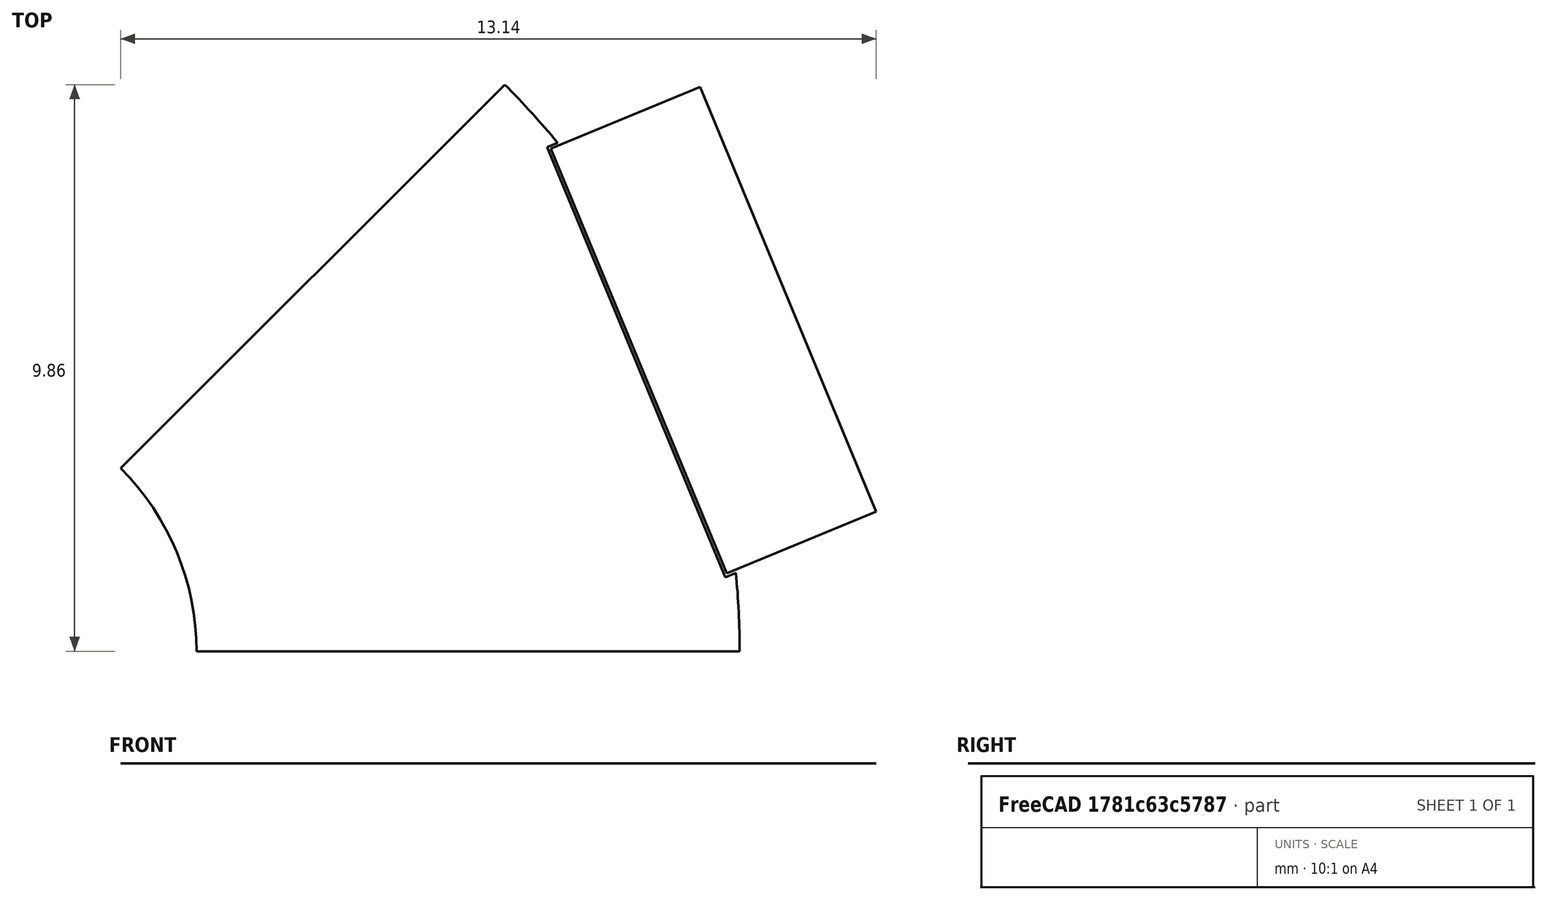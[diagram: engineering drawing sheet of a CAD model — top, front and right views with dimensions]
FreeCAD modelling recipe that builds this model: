
FCSTD DOCUMENT  (FreeCAD 0.18R4 (GitTag))
Label: rotor5
License: All rights reserved
LicenseURL: http://en.wikipedia.org/wiki/All_rights_reserved
objects: Sketcher::SketchObject×5, PartDesign::Body×2, Surface::Filling×2, Spreadsheet::Sheet×1
note: 9 computed .brp shape members not serialized (recipe doc carries the construction recipe); baked Part::Feature solids carry a one-line shape summary decoded from their .brp

FEATURE [Spreadsheet::Sheet] Spreadsheet  label="Variables"
  cells = A2=poleNumber; B2(poleNumber)=8; A3=outerDiameter; B3(outerDiameter)=33; D3=Calc Value; A4=innerDiameter; B4(innerDiameter)=9; D4=Input Value; A5=stackLength; B5(stackLength)=20; A6=stackingFactor; B6(stackingFactor)=0.95; A7=embrace; B7(embrace)=70; A8=contourRatio; B8(contourRatio)=80; A9=magnetAirgap; B9(magnetAirgap)=0.05; A10=poleSeparation; B10(poleSeparation)=2; A11=magnetWidth; B11(magnetWidth)=8; A12=magnetHeight; B12(magnetHeight)=2.8; A13=rib; B13(rib)=0.5; A14=bridgeCurved; B14(bridgeCurved)=0.5; A15=cutTop; B15(cutTop)=0.2; A16=cutBottom; B16(cutBottom)=0.25; A17=segmentAngle; B17(segmentAngle)==360 / poleNumber; A18=movePocketInwards; B18(movePocketInwards)=0.5; A19=cuttingThickness; B19(cuttingThickness)=0.1; A20=magnetLength; B20(magnetLength)==stackLength; A21=cut; B21(cut)=0.2; A22=ribShaft; B22(ribShaft)=0.5; A23=magnetEmbrace; B23(magnetEmbrace)=70; A24=magnetContourRatio; B24(magnetContourRatio)=95; A25=axialMisalignment; B25(axialMisalignment)=0.5
FEATURE [Sketcher::SketchObject] Sketch003  label="RotorSketch"
  MapMode = 5
  Support = -> [XY_Plane]
  expr: Constraints[33] = Variables.magnetWidth + 2 * Variables.magnetAirgap
  expr: Constraints[15] = Variables.outerDiameter / 2
  expr: Constraints[32] = Spreadsheet.cut
  expr: Constraints[50] = Variables.magnetHeight + Variables.magnetAirgap
  expr: Constraints[18] = Variables.segmentAngle / 2
  expr: Constraints[0] = Variables.segmentAngle
  expr: Constraints[14] = Variables.innerDiameter / 2
  sketch-geometry (19):
    g0: LineSegment [constr] StartX=4.5 StartY=0 StartZ=0 EndX=16.5 EndY=0 EndZ=0
    g1: LineSegment [constr] StartX=3.18198 StartY=3.18198 StartZ=0 EndX=11.6673 EndY=11.6673 EndZ=0
    g2: LineSegment [constr] StartX=0 StartY=0 StartZ=0 EndX=4.5 EndY=0 EndZ=0
    g3: LineSegment [constr] StartX=0 StartY=0 StartZ=0 EndX=3.18198 EndY=3.18198 EndZ=0
    g4: ArcOfCircle [constr] CenterX=0 CenterY=0 CenterZ=0 NormalX=0 NormalY=0 NormalZ=1 AngleXU=0 Radius=16.5 StartAngle=0 EndAngle=0.785398
    g5: ArcOfCircle CenterX=0 CenterY=0 CenterZ=0 NormalX=0 NormalY=0 NormalZ=1 AngleXU=0 Radius=4.5 StartAngle=0 EndAngle=0.785398
    g6: LineSegment [constr] StartX=0 StartY=0 StartZ=0 EndX=15.244 EndY=6.31428 EndZ=0
    g7: LineSegment [constr] StartX=0 StartY=0 StartZ=0 EndX=12.7091 EndY=10.5228 EndZ=0
    g8: LineSegment [constr] StartX=0 StartY=0 StartZ=0 EndX=16.4274 EndY=1.54594 EndZ=0
    g9: LineSegment [constr] StartX=0 StartY=0 StartZ=0 EndX=10.5947 EndY=8.77218 EndZ=0
    g10: LineSegment [constr] StartX=0 StartY=0 StartZ=0 EndX=13.6945 EndY=1.28875 EndZ=0
    g11: LineSegment StartX=10.5947 StartY=8.77218 StartZ=0 EndX=13.6945 EndY=1.28875 EndZ=0
    g12: LineSegment StartX=10.5947 StartY=8.77218 StartZ=0 EndX=10.7795 EndY=8.84871 EndZ=0
    g13: ArcOfCircle CenterX=0 CenterY=0 CenterZ=0 NormalX=0 NormalY=0 NormalZ=1 AngleXU=0 Radius=13.9462 StartAngle=0.687345 EndAngle=0.785398
    g14: LineSegment StartX=3.18198 StartY=3.18198 StartZ=0 EndX=9.86148 EndY=9.86148 EndZ=0
    g15: LineSegment StartX=4.5 StartY=0 StartZ=0 EndX=13.9462 EndY=0 EndZ=0
    g16: LineSegment StartX=13.6945 StartY=1.28875 StartZ=0 EndX=13.8793 EndY=1.36529 EndZ=0
    g17: ArcOfCircle CenterX=0 CenterY=0 CenterZ=0 NormalX=0 NormalY=0 NormalZ=1 AngleXU=0 Radius=13.9462 StartAngle=0 EndAngle=0.0980535
    g18: LineSegment [constr] StartX=10.5947 StartY=8.77218 StartZ=0 EndX=13.2278 EndY=9.86282 EndZ=0
  constraints (51):
    c: Angle(g0,g1) = 0.785398
    c: Coincident(g2,g-1)
    c: Coincident(g2,g0)
    c: Coincident(g3,g2)
    c: Coincident(g3,g1)
    c: Parallel(g2,g0)
    c: Parallel(g3,g1)
    c: Coincident(g4,g-1)
    c: Coincident(g4,g0)
    c: Coincident(g4,g1)
    c: Coincident(g5,g4)
    c: Coincident(g5,g1)
    c: Coincident(g5,g0)
    c: Angle(g-1,g2) = 0
    c: Radius(g5) = 4.5
    c: Radius(g4) = 16.5
    c: Coincident(g6,g5)
    c: PointOnObject(g6,g4)
    c: Angle(g-1,g6) = 0.392699
    c: Coincident(g7,g5)
    c: PointOnObject(g7,g4)
    c: Coincident(g8,g5)
    c: Symmetric(g7,g8,g6)
    c: Coincident(g9,g5)
    c: PointOnObject(g9,g7)
    c: Coincident(g10,g5)
    c: PointOnObject(g10,g8)
    c: Equal(g9,g10)
    c: Coincident(g11,g9)
    c: Coincident(g11,g10)
    c: Coincident(g12,g11)
    c: Angle(g11,g12) = 1.5708
    c: Distance(g12) = 0.2
    c: Distance(g11) = 8.1
    c: Coincident(g13,g5)
    c: Coincident(g13,g12)
    c: PointOnObject(g13,g1)
    c: PointOnObject(g15,g0)
    c: Coincident(g14,g5)
    c: Coincident(g14,g13)
    c: Coincident(g15,g5)
    c: Coincident(g16,g11)
    c: Angle(g16,g11) = 1.5708
    c: Equal(g16,g12)
    c: Coincident(g17,g5)
    c: Coincident(g17,g15)
    c: Coincident(g17,g16)
    c: Coincident(g18,g11)
    c: PointOnObject(g18,g4)
    c: Angle(g11,g18) = 1.5708
    c: Distance(g18) = 2.85
FEATURE [Sketcher::SketchObject] Sketch004  label="BoundingBox"
  MapMode = 5
  Support = -> [XY_Plane]
  expr: Constraints[8] = Variables.outerDiameter
  sketch-geometry (6):
    g0: LineSegment StartX=-16.5 StartY=-16.5 StartZ=0 EndX=16.5 EndY=-16.5 EndZ=0
    g1: LineSegment StartX=16.5 StartY=-16.5 StartZ=0 EndX=16.5 EndY=16.5 EndZ=0
    g2: LineSegment StartX=16.5 StartY=16.5 StartZ=0 EndX=-16.5 EndY=16.5 EndZ=0
    g3: LineSegment StartX=-16.5 StartY=16.5 StartZ=0 EndX=-16.5 EndY=-16.5 EndZ=0
    g4: LineSegment [constr] StartX=-16.5 StartY=-16.5 StartZ=0 EndX=16.5 EndY=16.5 EndZ=0
    g5: GeomPoint X=0 Y=0 Z=0
  constraints (14):
    c: Coincident(g0,g1)
    c: Coincident(g1,g2)
    c: Coincident(g2,g3)
    c: Coincident(g3,g0)
    c: Horizontal(g0)
    c: Horizontal(g2)
    c: Vertical(g1)
    c: Vertical(g3)
    c: DistanceY(g1,g1) = 33
    c: Equal(g2,g1)
    c: Coincident(g4,g0)
    c: Coincident(g4,g1)
    c: Symmetric(g0,g1,g5)
    c: Coincident(g-1,g5)
FEATURE [Sketcher::SketchObject] Sketch005  label="RotorSideSketch"
  MapMode = 5
  Support = -> [XY_Plane001]
  expr: Constraints[21] = Variables.stackLength / 2 - Variables.axialMisalignment
  expr: Constraints[9] = Variables.outerDiameter / 2
  expr: Constraints[8] = Variables.innerDiameter / 2
  expr: Constraints[7] = Variables.stackLength
  sketch-geometry (8):
    g0: LineSegment StartX=-9.5 StartY=4.5 StartZ=0 EndX=10.5 EndY=4.5 EndZ=0
    g1: LineSegment StartX=10.5 StartY=4.5 StartZ=0 EndX=10.5 EndY=16.5 EndZ=0
    g2: LineSegment StartX=10.5 StartY=16.5 StartZ=0 EndX=-9.5 EndY=16.5 EndZ=0
    g3: LineSegment StartX=-9.5 StartY=16.5 StartZ=0 EndX=-9.5 EndY=4.5 EndZ=0
    g4: LineSegment StartX=-9.5 StartY=-4.5 StartZ=0 EndX=10.5 EndY=-4.5 EndZ=0
    g5: LineSegment StartX=10.5 StartY=-4.5 StartZ=0 EndX=10.5 EndY=-16.5 EndZ=0
    g6: LineSegment StartX=10.5 StartY=-16.5 StartZ=0 EndX=-9.5 EndY=-16.5 EndZ=0
    g7: LineSegment StartX=-9.5 StartY=-16.5 StartZ=0 EndX=-9.5 EndY=-4.5 EndZ=0
  constraints (23):
    c: Coincident(g0,g1)
    c: Coincident(g1,g2)
    c: Coincident(g2,g3)
    c: Coincident(g3,g0)
    c: Horizontal(g0)
    c: Vertical(g1)
    c: Vertical(g3)
    c: DistanceX(g2,g2) = 20
    c: DistanceY(g-1,g0) = 4.5
    c: DistanceY(g-1,g1) = 16.5
    c: Coincident(g4,g5)
    c: Coincident(g5,g6)
    c: Coincident(g6,g7)
    c: Coincident(g7,g4)
    c: Horizontal(g4)
    c: Vertical(g5)
    c: Vertical(g7)
    c: Equal(g4,g0)
    c: Equal(g7,g3)
    c: Horizontal(g6)
    c: Horizontal(g2)
    c: DistanceX(g0,g-1) = 9.5
    c: Symmetric(g4,g0,g-1)
FEATURE [Sketcher::SketchObject] Sketch006  label="MagnetSideSketch"
  ExternalGeometry = -> [Sketch005]
  MapMode = 5
  Support = -> [XY_Plane001]
  expr: Constraints[20] = Variables.stackLength / 2 - Variables.axialMisalignment
  expr: Constraints[7] = Variables.magnetHeight
  sketch-geometry (8):
    g0: LineSegment StartX=-9.5 StartY=13.7 StartZ=0 EndX=10.5 EndY=13.7 EndZ=0
    g1: LineSegment StartX=10.5 StartY=13.7 StartZ=0 EndX=10.5 EndY=16.5 EndZ=0
    g2: LineSegment StartX=10.5 StartY=16.5 StartZ=0 EndX=-9.5 EndY=16.5 EndZ=0
    g3: LineSegment StartX=-9.5 StartY=16.5 StartZ=0 EndX=-9.5 EndY=13.7 EndZ=0
    g4: LineSegment StartX=-9.5 StartY=-16.5 StartZ=0 EndX=10.5 EndY=-16.5 EndZ=0
    g5: LineSegment StartX=10.5 StartY=-16.5 StartZ=0 EndX=10.5 EndY=-13.7 EndZ=0
    g6: LineSegment StartX=10.5 StartY=-13.7 StartZ=0 EndX=-9.5 EndY=-13.7 EndZ=0
    g7: LineSegment StartX=-9.5 StartY=-13.7 StartZ=0 EndX=-9.5 EndY=-16.5 EndZ=0
  constraints (21):
    c: Coincident(g0,g1)
    c: Coincident(g1,g2)
    c: Coincident(g2,g3)
    c: Coincident(g3,g0)
    c: Horizontal(g0)
    c: Vertical(g1)
    c: Vertical(g3)
    c: DistanceY(g1,g1) = 2.8
    c: Coincident(g4,g5)
    c: Coincident(g5,g6)
    c: Coincident(g6,g7)
    c: Coincident(g7,g4)
    c: Horizontal(g4)
    c: Vertical(g5)
    c: Vertical(g7)
    c: Symmetric(g6,g0,g-1)
    c: Symmetric(g5,g0,g-1)
    c: Equal(g7,g3)
    c: Coincident(g1,g-3)
    c: Horizontal(g2)
    c: DistanceX(g0,g-1) = 9.5
FEATURE [PartDesign::Body] Body001  label="SideView"
  Group = -> [Sketch005,Sketch006]
  Origin = -> Origin001
FEATURE [Surface::Filling] Surface  label="Rotor_Surface"
  Anisotropy = false
  BoundaryEdges = -> [Sketch003]
  BoundaryOrder = [0,0,0,0,0,0,0,0]
  Degree = 3
  Iterations = 2
  MaximumDegree = 8
  MaximumSegments = 9
  PointsOnCurve = 15
  TolAngular = 0.01
  TolCurvature = 0.1
  Tolerance2d = 1e-05
  Tolerance3d = 0.0001
FEATURE [Sketcher::SketchObject] Sketch007  label="MagnetSketch"
  MapMode = 5
  Support = -> [XY_Plane]
  expr: Constraints[55] = Variables.magnetAirgap
  expr: Constraints[14] = Variables.innerDiameter / 2
  expr: Constraints[33] = Variables.magnetWidth + 2 * Variables.magnetAirgap
  expr: Constraints[15] = Variables.outerDiameter / 2
  expr: Constraints[32] = Spreadsheet.cut
  expr: Constraints[50] = Variables.magnetHeight + Variables.magnetAirgap
  expr: Constraints[18] = Variables.segmentAngle / 2
  expr: Constraints[0] = Variables.segmentAngle
  sketch-geometry (25):
    g0: LineSegment [constr] StartX=4.5 StartY=0 StartZ=0 EndX=16.5 EndY=0 EndZ=0
    g1: LineSegment [constr] StartX=3.18198 StartY=3.18198 StartZ=0 EndX=11.6673 EndY=11.6673 EndZ=0
    g2: LineSegment [constr] StartX=0 StartY=0 StartZ=0 EndX=4.5 EndY=0 EndZ=0
    g3: LineSegment [constr] StartX=0 StartY=0 StartZ=0 EndX=3.18198 EndY=3.18198 EndZ=0
    g4: ArcOfCircle [constr] CenterX=0 CenterY=0 CenterZ=0 NormalX=0 NormalY=0 NormalZ=1 AngleXU=0 Radius=16.5 StartAngle=0 EndAngle=0.785398
    g5: ArcOfCircle [constr] CenterX=0 CenterY=0 CenterZ=0 NormalX=0 NormalY=0 NormalZ=1 AngleXU=0 Radius=4.5 StartAngle=0 EndAngle=0.785398
    g6: LineSegment [constr] StartX=0 StartY=0 StartZ=0 EndX=15.244 EndY=6.31428 EndZ=0
    g7: LineSegment [constr] StartX=0 StartY=0 StartZ=0 EndX=12.7091 EndY=10.5228 EndZ=0
    g8: LineSegment [constr] StartX=0 StartY=0 StartZ=0 EndX=16.4274 EndY=1.54594 EndZ=0
    g9: LineSegment [constr] StartX=0 StartY=0 StartZ=0 EndX=10.5947 EndY=8.77218 EndZ=0
    g10: LineSegment [constr] StartX=0 StartY=0 StartZ=0 EndX=13.6945 EndY=1.28875 EndZ=0
    g11: LineSegment [constr] StartX=10.5947 StartY=8.77218 StartZ=0 EndX=13.6945 EndY=1.28875 EndZ=0
    g12: LineSegment [constr] StartX=10.5947 StartY=8.77218 StartZ=0 EndX=10.7795 EndY=8.84871 EndZ=0
    g13: ArcOfCircle [constr] CenterX=0 CenterY=0 CenterZ=0 NormalX=0 NormalY=0 NormalZ=1 AngleXU=0 Radius=13.9462 StartAngle=0.687345 EndAngle=0.785398
    g14: LineSegment [constr] StartX=3.18198 StartY=3.18198 StartZ=0 EndX=9.86148 EndY=9.86148 EndZ=0
    g15: LineSegment [constr] StartX=4.5 StartY=0 StartZ=0 EndX=13.9462 EndY=0 EndZ=0
    g16: LineSegment StartX=13.6945 StartY=1.28875 StartZ=0 EndX=13.8793 EndY=1.36529 EndZ=0
    g17: ArcOfCircle [constr] CenterX=0 CenterY=0 CenterZ=0 NormalX=0 NormalY=0 NormalZ=1 AngleXU=0 Radius=13.9462 StartAngle=0 EndAngle=0.0980535
    g18: LineSegment [constr] StartX=10.5947 StartY=8.77218 StartZ=0 EndX=13.2278 EndY=9.86282 EndZ=0
    g19: LineSegment StartX=10.6601 StartY=8.74512 StartZ=0 EndX=13.7215 EndY=1.35408 EndZ=0
    g20: LineSegment [constr] StartX=10.6601 StartY=8.74512 StartZ=0 EndX=10.6139 EndY=8.72598 EndZ=0
    g21: LineSegment StartX=13.2586 StartY=9.82144 StartZ=0 EndX=10.6601 EndY=8.74512 EndZ=0
    g22: LineSegment [constr] StartX=10.6601 StartY=8.74512 StartZ=0 EndX=10.6409 EndY=8.79131 EndZ=0
    g23: LineSegment StartX=13.7215 StartY=1.35408 StartZ=0 EndX=16.32 EndY=2.43041 EndZ=0
    g24: LineSegment StartX=13.2586 StartY=9.82144 StartZ=0 EndX=16.32 EndY=2.43041 EndZ=0
  constraints (68):
    c: Angle(g0,g1) = 0.785398
    c: Coincident(g2,g-1)
    c: Coincident(g2,g0)
    c: Coincident(g3,g2)
    c: Coincident(g3,g1)
    c: Parallel(g2,g0)
    c: Parallel(g3,g1)
    c: Coincident(g4,g-1)
    c: Coincident(g4,g0)
    c: Coincident(g4,g1)
    c: Coincident(g5,g4)
    c: Coincident(g5,g1)
    c: Coincident(g5,g0)
    c: Angle(g-1,g2) = 0
    c: Radius(g5) = 4.5
    c: Radius(g4) = 16.5
    c: Coincident(g6,g5)
    c: PointOnObject(g6,g4)
    c: Angle(g-1,g6) = 0.392699
    c: Coincident(g7,g5)
    c: PointOnObject(g7,g4)
    c: Coincident(g8,g5)
    c: Symmetric(g7,g8,g6)
    c: Coincident(g9,g5)
    c: PointOnObject(g9,g7)
    c: Coincident(g10,g5)
    c: PointOnObject(g10,g8)
    c: Equal(g9,g10)
    c: Coincident(g11,g9)
    c: Coincident(g11,g10)
    c: Coincident(g12,g11)
    c: Angle(g11,g12) = 1.5708
    c: Distance(g12) = 0.2
    c: Distance(g11) = 8.1
    c: Coincident(g13,g5)
    c: Coincident(g13,g12)
    c: PointOnObject(g13,g1)
    c: PointOnObject(g15,g0)
    c: Coincident(g14,g5)
    c: Coincident(g14,g13)
    c: Coincident(g15,g5)
    c: Coincident(g16,g11)
    c: Angle(g16,g11) = 1.5708
    c: Equal(g16,g12)
    c: Coincident(g17,g5)
    c: Coincident(g17,g15)
    c: Coincident(g17,g16)
    c: Coincident(g18,g11)
    c: PointOnObject(g18,g4)
    c: Angle(g11,g18) = 1.5708
    c: Distance(g18) = 2.85
    c: Parallel(g19,g11)
    c: Coincident(g20,g19)
    c: PointOnObject(g20,g11)
    c: Angle(g20,g19) = 1.5708
    c: Distance(g20) = 0.05
    c: PointOnObject(g21,g4)
    c: Angle(g19,g21) = 1.5708
    c: Coincident(g19,g21)
    c: Coincident(g22,g19)
    c: PointOnObject(g22,g12)
    c: Angle(g22,g20) = 1.5708
    c: Equal(g22,g20)
    c: Symmetric(g21,g23,g6)
    c: Parallel(g23,g21)
    c: Coincident(g24,g21)
    c: Coincident(g24,g23)
    c: Coincident(g19,g23)
FEATURE [PartDesign::Body] Body  label="TopView"
  Group = -> [Sketch003,Sketch004,Sketch007]
  Origin = -> Origin
FEATURE [Surface::Filling] Surface001  label="Magnet_Surface"
  Anisotropy = false
  BoundaryEdges = -> [Sketch007]
  BoundaryOrder = [0,0,0,0]
  Degree = 3
  Iterations = 2
  MaximumDegree = 8
  MaximumSegments = 9
  PointsOnCurve = 15
  TolAngular = 0.01
  TolCurvature = 0.1
  Tolerance2d = 1e-05
  Tolerance3d = 0.0001
